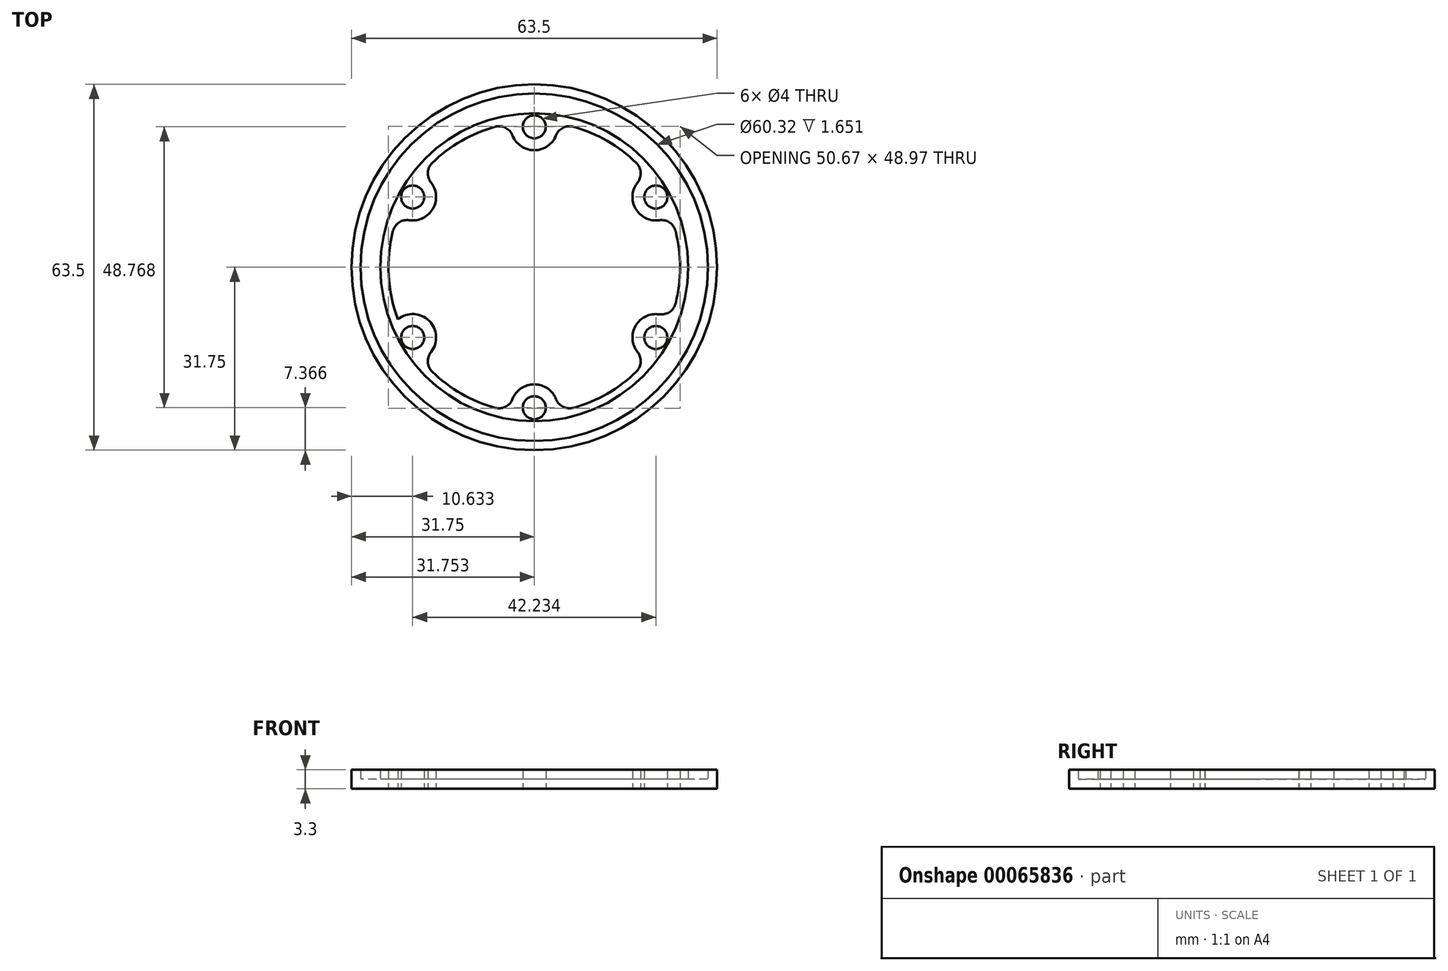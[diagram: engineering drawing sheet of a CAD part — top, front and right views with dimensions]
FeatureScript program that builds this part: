
annotation { "Feature Type Name" : "Feature", "Feature Type Description" : "" }
export const myFeature = defineFeature(function(context is Context, id is Id, definition is map)
    precondition{}
    {
        {
            var Q0;
            Q0=qCreatedBy(makeId("Top.planeOp"),FACE);
            var sketch = newSketch(context, id + "F0", { "sketchPlane" : qUnion([Q0])});
            skCircle(sketch, "E0", {"center": v(0, 0) * mm, "radius": 31.75 * mm});
            skCircle(sketch, "E1", {"center": v(0, 0) * mm, "radius": 25.34 * mm});
            skSolve(sketch);
        }
        {
            var Q0;
            Q0=makeQuery(id+"F0.imprint","IMPRINT",FACE,{"disambiguationData":[TD([[makeQuery(id+"F0.imprint","IMPRINT",EDGE,{"derivedFrom":sQuery(id+"F0.wireOp",EDGE,"E0")}),1.0]])]});
            extrude(context, id + "F1", {"entities" : qUnion([Q0]), "depth" : 1.65 * mm});
        }
        {
            var Q0;
            Q0=makeQuery(id+"F1.opExtrude","CAP_FACE",FACE,{"disambiguationData":[OSD([sQuery(id+"F0.wireOp",EDGE,"E0"),sQuery(id+"F0.wireOp",EDGE,"E1")])],"isStart":false});
            var sketch = newSketch(context, id + "F2", { "sketchPlane" : qUnion([Q0])});
            skCircle(sketch, "E2", {"center": v(0, 0) * mm, "radius": 30.16 * mm});
            skCircle(sketch, "E3", {"center": v(0, 0) * mm, "radius": 26.73 * mm});
            skSolve(sketch);
        }
        {
            var Q0;
            Q0=makeQuery(id+"F2.imprint","IMPRINT",FACE,{"disambiguationData":[TD([[makeQuery(id+"F2.imprint","IMPRINT",EDGE,{"derivedFrom":sQuery(id+"F2.wireOp",EDGE,"E2")}),-1.0]])]});
            var Q1;
            Q1=makeQuery(id+"F2.imprint","IMPRINT",FACE,{"disambiguationData":[TD([[makeQuery(id+"F2.imprint","IMPRINT",EDGE,{"derivedFrom":sQuery(id+"F2.wireOp",EDGE,"E3")}),1.0]])]});
            extrude(context, id + "F3", {"entities" : qUnion([Q0, Q1]), "operationType" : NewBodyOperationType.ADD, "depth" : 1.65 * mm});
        }
        {
            var Q0;
            Q0=makeQuery(id+"F0.imprint","IMPRINT",FACE,{"disambiguationData":[TD([[makeQuery(id+"F0.imprint","IMPRINT",EDGE,{"derivedFrom":sQuery(id+"F0.wireOp",EDGE,"E0")}),1.0]])]});
            var sketch = newSketch(context, id + "F4", { "sketchPlane" : qUnion([Q0])});
            skCircle(sketch, "E4", {"center": v(0, 0) * mm, "radius": 24.38 * mm, "construction": true});
            skCircle(sketch, "E5", {"center": v(0, 24.38) * mm, "radius": 2 * mm});
            skCircle(sketch, "E6.1.0", {"center": v(-21.12, 12.2) * mm, "radius": 2 * mm});
            skCircle(sketch, "E6.2.0", {"center": v(-21.12, -12.2) * mm, "radius": 2 * mm});
            skCircle(sketch, "E6.3.0", {"center": v(0, -24.38) * mm, "radius": 2 * mm});
            skCircle(sketch, "E6.4.0", {"center": v(21.12, -12.2) * mm, "radius": 2 * mm});
            skCircle(sketch, "E6.5.0", {"center": v(21.12, 12.2) * mm, "radius": 2 * mm});
            skCircle(sketch, "E7", {"center": v(0, 24.38) * mm, "radius": 4.06 * mm});
            skCircle(sketch, "E8.1.0", {"center": v(-21.12, 12.2) * mm, "radius": 4.06 * mm});
            skCircle(sketch, "E8.2.0", {"center": v(-21.12, -12.2) * mm, "radius": 4.06 * mm});
            skCircle(sketch, "E8.3.0", {"center": v(0, -24.38) * mm, "radius": 4.06 * mm});
            skCircle(sketch, "E8.4.0", {"center": v(21.12, -12.2) * mm, "radius": 4.06 * mm});
            skCircle(sketch, "E8.5.0", {"center": v(21.12, 12.2) * mm, "radius": 4.06 * mm});
            skSolve(sketch);
        }
        {
            var Q0;
            {var subQ0=sQuery(id+"F4.wireOp",EDGE,"E6.3.0");var subQ1=makeQuery(id+"F0.imprint","IMPRINT",EDGE,{"derivedFrom":sQuery(id+"F0.wireOp",EDGE,"E1")});var subQ2=makeQuery(id+"F4.imprint","INTERSECT",VERTEX,{"disambiguationData":[OD(0.0)],"derivedFrom":[subQ1,subQ0]});Q0=makeQuery(id+"F4.imprint","IMPRINT",FACE,{"disambiguationData":[TD([[makeQuery(id+"F4.imprint","IMPRINT",EDGE,{"disambiguationData":[TD([[subQ2,1.0]])],"derivedFrom":subQ0}),-1.0]])]});}
            var Q1;
            {var subQ0=sQuery(id+"F4.wireOp",EDGE,"E6.4.0");var subQ1=makeQuery(id+"F0.imprint","IMPRINT",EDGE,{"derivedFrom":sQuery(id+"F0.wireOp",EDGE,"E1")});var subQ2=makeQuery(id+"F4.imprint","INTERSECT",VERTEX,{"disambiguationData":[OD(0.0)],"derivedFrom":[subQ1,subQ0]});Q1=makeQuery(id+"F4.imprint","IMPRINT",FACE,{"disambiguationData":[TD([[makeQuery(id+"F4.imprint","IMPRINT",EDGE,{"disambiguationData":[TD([[subQ2,1.0]])],"derivedFrom":subQ0}),-1.0]])]});}
            var Q2;
            {var subQ0=sQuery(id+"F4.wireOp",EDGE,"E6.2.0");var subQ1=makeQuery(id+"F0.imprint","IMPRINT",EDGE,{"derivedFrom":sQuery(id+"F0.wireOp",EDGE,"E1")});var subQ2=makeQuery(id+"F4.imprint","INTERSECT",VERTEX,{"disambiguationData":[OD(0.0)],"derivedFrom":[subQ1,subQ0]});Q2=makeQuery(id+"F4.imprint","IMPRINT",FACE,{"disambiguationData":[TD([[makeQuery(id+"F4.imprint","IMPRINT",EDGE,{"disambiguationData":[TD([[subQ2,1.0]])],"derivedFrom":subQ0}),-1.0]])]});}
            var Q3;
            {var subQ0=sQuery(id+"F4.wireOp",EDGE,"E6.1.0");var subQ1=makeQuery(id+"F0.imprint","IMPRINT",EDGE,{"derivedFrom":sQuery(id+"F0.wireOp",EDGE,"E1")});var subQ2=makeQuery(id+"F4.imprint","INTERSECT",VERTEX,{"disambiguationData":[OD(0.0)],"derivedFrom":[subQ1,subQ0]});Q3=makeQuery(id+"F4.imprint","IMPRINT",FACE,{"disambiguationData":[TD([[makeQuery(id+"F4.imprint","IMPRINT",EDGE,{"disambiguationData":[TD([[subQ2,-1.0]])],"derivedFrom":subQ0}),-1.0]])]});}
            var Q4;
            {var subQ0=sQuery(id+"F4.wireOp",EDGE,"E6.5.0");var subQ1=makeQuery(id+"F0.imprint","IMPRINT",EDGE,{"derivedFrom":sQuery(id+"F0.wireOp",EDGE,"E1")});var subQ2=makeQuery(id+"F4.imprint","INTERSECT",VERTEX,{"disambiguationData":[OD(0.0)],"derivedFrom":[subQ1,subQ0]});Q4=makeQuery(id+"F4.imprint","IMPRINT",FACE,{"disambiguationData":[TD([[makeQuery(id+"F4.imprint","IMPRINT",EDGE,{"disambiguationData":[TD([[subQ2,-1.0]])],"derivedFrom":subQ0}),-1.0]])]});}
            var Q5;
            {var subQ0=sQuery(id+"F4.wireOp",EDGE,"E5");var subQ1=makeQuery(id+"F0.imprint","IMPRINT",EDGE,{"derivedFrom":sQuery(id+"F0.wireOp",EDGE,"E1")});var subQ2=makeQuery(id+"F4.imprint","INTERSECT",VERTEX,{"disambiguationData":[OD(0.0)],"derivedFrom":[subQ1,subQ0]});Q5=makeQuery(id+"F4.imprint","IMPRINT",FACE,{"disambiguationData":[TD([[makeQuery(id+"F4.imprint","IMPRINT",EDGE,{"disambiguationData":[TD([[subQ2,-1.0]])],"derivedFrom":subQ0}),-1.0]])]});}
            extrude(context, id + "F5", {"entities" : qUnion([Q0, Q1, Q2, Q3, Q4, Q5]), "operationType" : NewBodyOperationType.ADD, "depth" : 3.3 * mm});
        }
        {
            var Q0;
            {var subQ0=sQuery(id+"F4.wireOp",EDGE,"E8.1.0");var subQ1=sQuery(id+"F0.wireOp",EDGE,"E1");Q0=makeQuery(id+"F5.opExtrude","SWEPT_EDGE",EDGE,{"disambiguationData":[OSD([subQ1,subQ0]),TDD([makeQuery(id+"F4.imprint","INTERSECT",VERTEX,{"disambiguationData":[OD(0.0)],"derivedFrom":[makeQuery(id+"F0.imprint","IMPRINT",EDGE,{"derivedFrom":subQ1}),subQ0]})])]});}
            var Q1;
            {var subQ0=sQuery(id+"F4.wireOp",EDGE,"E8.1.0");var subQ1=sQuery(id+"F0.wireOp",EDGE,"E1");Q1=makeQuery(id+"F5.opExtrude","SWEPT_EDGE",EDGE,{"disambiguationData":[OSD([subQ1,subQ0]),TDD([makeQuery(id+"F4.imprint","INTERSECT",VERTEX,{"disambiguationData":[OD(1.0)],"derivedFrom":[makeQuery(id+"F0.imprint","IMPRINT",EDGE,{"derivedFrom":subQ1}),subQ0]})])]});}
            var Q2;
            {var subQ0=sQuery(id+"F4.wireOp",EDGE,"E8.2.0");var subQ1=sQuery(id+"F0.wireOp",EDGE,"E1");Q2=makeQuery(id+"F5.opExtrude","SWEPT_EDGE",EDGE,{"disambiguationData":[OSD([subQ1,subQ0]),TDD([makeQuery(id+"F4.imprint","INTERSECT",VERTEX,{"disambiguationData":[OD(1.0)],"derivedFrom":[makeQuery(id+"F0.imprint","IMPRINT",EDGE,{"derivedFrom":subQ1}),subQ0]})])]});}
            var Q3;
            {var subQ0=sQuery(id+"F4.wireOp",EDGE,"E7");var subQ1=sQuery(id+"F0.wireOp",EDGE,"E1");Q3=makeQuery(id+"F5.opExtrude","SWEPT_EDGE",EDGE,{"disambiguationData":[OSD([subQ1,subQ0]),TDD([makeQuery(id+"F4.imprint","INTERSECT",VERTEX,{"disambiguationData":[OD(1.0)],"derivedFrom":[makeQuery(id+"F0.imprint","IMPRINT",EDGE,{"derivedFrom":subQ1}),subQ0]})])]});}
            var Q4;
            {var subQ0=sQuery(id+"F4.wireOp",EDGE,"E7");var subQ1=sQuery(id+"F0.wireOp",EDGE,"E1");Q4=makeQuery(id+"F5.opExtrude","SWEPT_EDGE",EDGE,{"disambiguationData":[OSD([subQ1,subQ0]),TDD([makeQuery(id+"F4.imprint","INTERSECT",VERTEX,{"disambiguationData":[OD(0.0)],"derivedFrom":[makeQuery(id+"F0.imprint","IMPRINT",EDGE,{"derivedFrom":subQ1}),subQ0]})])]});}
            var Q5;
            {var subQ0=sQuery(id+"F4.wireOp",EDGE,"E8.5.0");var subQ1=sQuery(id+"F0.wireOp",EDGE,"E1");Q5=makeQuery(id+"F5.opExtrude","SWEPT_EDGE",EDGE,{"disambiguationData":[OSD([subQ1,subQ0]),TDD([makeQuery(id+"F4.imprint","INTERSECT",VERTEX,{"disambiguationData":[OD(0.0)],"derivedFrom":[makeQuery(id+"F0.imprint","IMPRINT",EDGE,{"derivedFrom":subQ1}),subQ0]})])]});}
            var Q6;
            {var subQ0=sQuery(id+"F4.wireOp",EDGE,"E8.5.0");var subQ1=sQuery(id+"F0.wireOp",EDGE,"E1");Q6=makeQuery(id+"F5.opExtrude","SWEPT_EDGE",EDGE,{"disambiguationData":[OSD([subQ1,subQ0]),TDD([makeQuery(id+"F4.imprint","INTERSECT",VERTEX,{"disambiguationData":[OD(1.0)],"derivedFrom":[makeQuery(id+"F0.imprint","IMPRINT",EDGE,{"derivedFrom":subQ1}),subQ0]})])]});}
            var Q7;
            {var subQ0=sQuery(id+"F4.wireOp",EDGE,"E8.3.0");var subQ1=sQuery(id+"F0.wireOp",EDGE,"E1");Q7=makeQuery(id+"F5.opExtrude","SWEPT_EDGE",EDGE,{"disambiguationData":[OSD([subQ1,subQ0]),TDD([makeQuery(id+"F4.imprint","INTERSECT",VERTEX,{"disambiguationData":[OD(1.0)],"derivedFrom":[makeQuery(id+"F0.imprint","IMPRINT",EDGE,{"derivedFrom":subQ1}),subQ0]})])]});}
            var Q8;
            {var subQ0=sQuery(id+"F4.wireOp",EDGE,"E8.3.0");var subQ1=sQuery(id+"F0.wireOp",EDGE,"E1");Q8=makeQuery(id+"F5.opExtrude","SWEPT_EDGE",EDGE,{"disambiguationData":[OSD([subQ1,subQ0]),TDD([makeQuery(id+"F4.imprint","INTERSECT",VERTEX,{"disambiguationData":[OD(0.0)],"derivedFrom":[makeQuery(id+"F0.imprint","IMPRINT",EDGE,{"derivedFrom":subQ1}),subQ0]})])]});}
            var Q9;
            {var subQ0=sQuery(id+"F4.wireOp",EDGE,"E8.4.0");var subQ1=sQuery(id+"F0.wireOp",EDGE,"E1");Q9=makeQuery(id+"F5.opExtrude","SWEPT_EDGE",EDGE,{"disambiguationData":[OSD([subQ1,subQ0]),TDD([makeQuery(id+"F4.imprint","INTERSECT",VERTEX,{"disambiguationData":[OD(1.0)],"derivedFrom":[makeQuery(id+"F0.imprint","IMPRINT",EDGE,{"derivedFrom":subQ1}),subQ0]})])]});}
            var Q10;
            {var subQ0=sQuery(id+"F4.wireOp",EDGE,"E8.4.0");var subQ1=sQuery(id+"F0.wireOp",EDGE,"E1");Q10=makeQuery(id+"F5.opExtrude","SWEPT_EDGE",EDGE,{"disambiguationData":[OSD([subQ1,subQ0]),TDD([makeQuery(id+"F4.imprint","INTERSECT",VERTEX,{"disambiguationData":[OD(0.0)],"derivedFrom":[makeQuery(id+"F0.imprint","IMPRINT",EDGE,{"derivedFrom":subQ1}),subQ0]})])]});}
            fillet(context, id + "F6", {"entities" : qUnion([Q0, Q1, Q2, Q3, Q4, Q5, Q6, Q7, Q8, Q9, Q10]), "radius" : 2.54 * mm, "tangentPropagation" : true, "allowEdgeOverflow" : false});
        }
        {
            var Q0;
            {var subQ0=sQuery(id+"F4.wireOp",EDGE,"E5");var subQ1=makeQuery(id+"F0.imprint","IMPRINT",EDGE,{"derivedFrom":sQuery(id+"F0.wireOp",EDGE,"E1")});var subQ2=makeQuery(id+"F4.imprint","INTERSECT",VERTEX,{"disambiguationData":[OD(0.0)],"derivedFrom":[subQ1,subQ0]});Q0=makeQuery(id+"F4.imprint","IMPRINT",FACE,{"disambiguationData":[TD([[makeQuery(id+"F4.imprint","IMPRINT",EDGE,{"disambiguationData":[TD([[subQ2,1.0]])],"derivedFrom":subQ0}),1.0]])]});}
            var Q1;
            {var subQ0=sQuery(id+"F4.wireOp",EDGE,"E6.5.0");var subQ1=makeQuery(id+"F0.imprint","IMPRINT",EDGE,{"derivedFrom":sQuery(id+"F0.wireOp",EDGE,"E1")});var subQ2=makeQuery(id+"F4.imprint","INTERSECT",VERTEX,{"disambiguationData":[OD(0.0)],"derivedFrom":[subQ1,subQ0]});Q1=makeQuery(id+"F4.imprint","IMPRINT",FACE,{"disambiguationData":[TD([[makeQuery(id+"F4.imprint","IMPRINT",EDGE,{"disambiguationData":[TD([[subQ2,1.0]])],"derivedFrom":subQ0}),1.0]])]});}
            var Q2;
            {var subQ0=sQuery(id+"F4.wireOp",EDGE,"E6.4.0");var subQ1=makeQuery(id+"F0.imprint","IMPRINT",EDGE,{"derivedFrom":sQuery(id+"F0.wireOp",EDGE,"E1")});var subQ2=makeQuery(id+"F4.imprint","INTERSECT",VERTEX,{"disambiguationData":[OD(0.0)],"derivedFrom":[subQ1,subQ0]});Q2=makeQuery(id+"F4.imprint","IMPRINT",FACE,{"disambiguationData":[TD([[makeQuery(id+"F4.imprint","IMPRINT",EDGE,{"disambiguationData":[TD([[subQ2,-1.0]])],"derivedFrom":subQ0}),1.0]])]});}
            var Q3;
            {var subQ0=sQuery(id+"F4.wireOp",EDGE,"E6.3.0");var subQ1=makeQuery(id+"F0.imprint","IMPRINT",EDGE,{"derivedFrom":sQuery(id+"F0.wireOp",EDGE,"E1")});var subQ2=makeQuery(id+"F4.imprint","INTERSECT",VERTEX,{"disambiguationData":[OD(0.0)],"derivedFrom":[subQ1,subQ0]});Q3=makeQuery(id+"F4.imprint","IMPRINT",FACE,{"disambiguationData":[TD([[makeQuery(id+"F4.imprint","IMPRINT",EDGE,{"disambiguationData":[TD([[subQ2,-1.0]])],"derivedFrom":subQ0}),1.0]])]});}
            var Q4;
            {var subQ0=sQuery(id+"F4.wireOp",EDGE,"E6.1.0");var subQ1=makeQuery(id+"F0.imprint","IMPRINT",EDGE,{"derivedFrom":sQuery(id+"F0.wireOp",EDGE,"E1")});var subQ2=makeQuery(id+"F4.imprint","INTERSECT",VERTEX,{"disambiguationData":[OD(0.0)],"derivedFrom":[subQ1,subQ0]});Q4=makeQuery(id+"F4.imprint","IMPRINT",FACE,{"disambiguationData":[TD([[makeQuery(id+"F4.imprint","IMPRINT",EDGE,{"disambiguationData":[TD([[subQ2,1.0]])],"derivedFrom":subQ0}),1.0]])]});}
            var Q5;
            {var subQ0=sQuery(id+"F4.wireOp",EDGE,"E6.2.0");var subQ1=makeQuery(id+"F0.imprint","IMPRINT",EDGE,{"derivedFrom":sQuery(id+"F0.wireOp",EDGE,"E1")});var subQ2=makeQuery(id+"F4.imprint","INTERSECT",VERTEX,{"disambiguationData":[OD(0.0)],"derivedFrom":[subQ1,subQ0]});Q5=makeQuery(id+"F4.imprint","IMPRINT",FACE,{"disambiguationData":[TD([[makeQuery(id+"F4.imprint","IMPRINT",EDGE,{"disambiguationData":[TD([[subQ2,-1.0]])],"derivedFrom":subQ0}),1.0]])]});}
            extrude(context, id + "F7", {"entities" : qUnion([Q0, Q1, Q2, Q3, Q4, Q5]), "operationType" : NewBodyOperationType.REMOVE, "depth" : 25.4 * mm});
        }
    });
